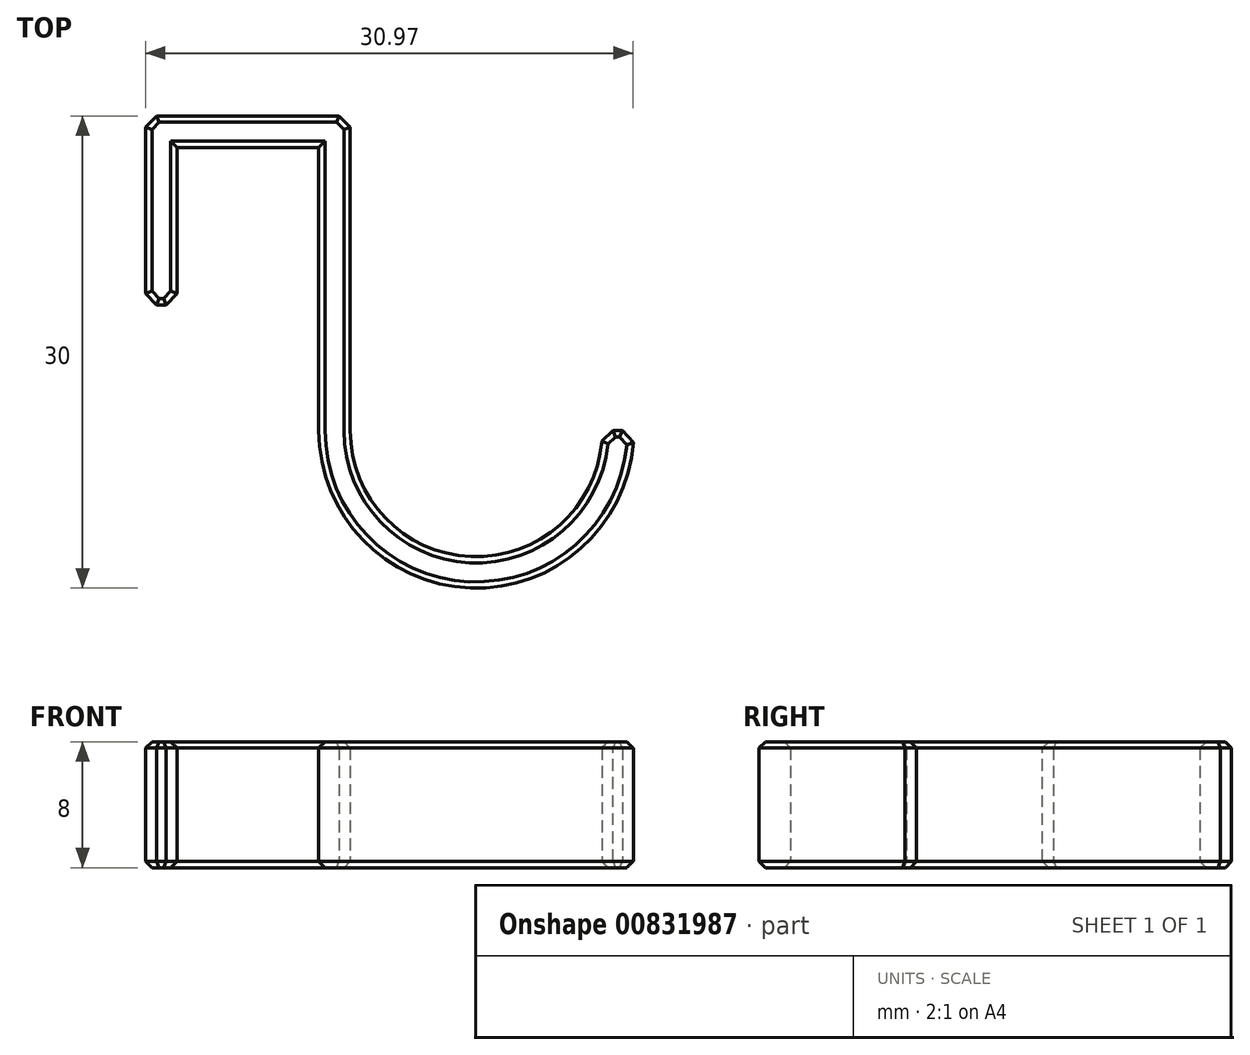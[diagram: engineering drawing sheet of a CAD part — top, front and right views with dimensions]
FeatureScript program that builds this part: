
annotation { "Feature Type Name" : "Feature", "Feature Type Description" : "" }
export const myFeature = defineFeature(function(context is Context, id is Id, definition is map)
    precondition{}
    {
        {
            var Q0;
            Q0=qCreatedBy(makeId("Top.planeOp"),FACE);
            var sketch = newSketch(context, id + "F0", { "sketchPlane" : qUnion([Q0])});
            skLineSegment(sketch, "E0", {"start": v(-19, 8) * mm, "end": v(-19, 18) * mm});
            skLineSegment(sketch, "E1", {"start": v(-19, 18) * mm, "end": v(-10, 18) * mm});
            skLineSegment(sketch, "E2", {"start": v(-10, 18) * mm, "end": v(-10, 0) * mm});
            skLineSegment(sketch, "E3", {"start": v(-19, 8) * mm, "end": v(-21, 8) * mm});
            skLineSegment(sketch, "E4", {"start": v(-21, 8) * mm, "end": v(-21, 20) * mm});
            skLineSegment(sketch, "E5", {"start": v(-21, 20) * mm, "end": v(-8, 20) * mm});
            skLineSegment(sketch, "E6", {"start": v(-8, 20) * mm, "end": v(-8, 0) * mm});
            skLineSegment(sketch, "E7", {"start": v(8, 0) * mm, "end": v(10, 0) * mm});
            skArc(sketch, "E8", {"start": v(-8, 0) * mm, "mid": v(0, -8) * mm, "end": v(8, 0) * mm});
            skArc(sketch, "E9", {"start": v(-10, 0) * mm, "mid": v(0, -10) * mm, "end": v(10, 0) * mm});
            skLineSegment(sketch, "E10", {"start": v(-19, 18) * mm, "end": v(-21, 18) * mm, "construction": true});
            skLineSegment(sketch, "E11", {"start": v(-10, 18) * mm, "end": v(-8, 18) * mm, "construction": true});
            skLineSegment(sketch, "E12", {"start": v(-10, 18) * mm, "end": v(-10, 20) * mm, "construction": true});
            skSolve(sketch);
        }
        {
            var Q0;
            Q0=makeQuery(id+"F0.imprint","IMPRINT",FACE,{"disambiguationData":[TD([[makeQuery(id+"F0.imprint","IMPRINT",EDGE,{"derivedFrom":sQuery(id+"F0.wireOp",EDGE,"E0")}),1.0]])]});
            extrude(context, id + "F1", {"entities" : qUnion([Q0]), "depth" : 8 * mm, "offsetDistance" : 25 * mm});
        }
        {
            var Q0;
            Q0=makeQuery(id+"F1.opExtrude","SWEPT_EDGE",EDGE,{"disambiguationData":[OSD([sQuery(id+"F0.wireOp",EDGE,"E5"),sQuery(id+"F0.wireOp",EDGE,"E6")])]});
            var Q1;
            Q1=makeQuery(id+"F1.opExtrude","SWEPT_EDGE",EDGE,{"disambiguationData":[OSD([sQuery(id+"F0.wireOp",EDGE,"E4"),sQuery(id+"F0.wireOp",EDGE,"E5")])]});
            var Q2;
            Q2=makeQuery(id+"F1.opExtrude","SWEPT_EDGE",EDGE,{"disambiguationData":[OSD([sQuery(id+"F0.wireOp",EDGE,"E3"),sQuery(id+"F0.wireOp",EDGE,"E4")])]});
            var Q3;
            Q3=makeQuery(id+"F1.opExtrude","SWEPT_EDGE",EDGE,{"disambiguationData":[OSD([sQuery(id+"F0.wireOp",EDGE,"E0"),sQuery(id+"F0.wireOp",EDGE,"E3")])]});
            var Q4;
            Q4=makeQuery(id+"F1.opExtrude","SWEPT_EDGE",EDGE,{"disambiguationData":[OSD([sQuery(id+"F0.wireOp",EDGE,"E7"),sQuery(id+"F0.wireOp",EDGE,"E9")])]});
            var Q5;
            Q5=makeQuery(id+"F1.opExtrude","SWEPT_EDGE",EDGE,{"disambiguationData":[OSD([sQuery(id+"F0.wireOp",EDGE,"E7"),sQuery(id+"F0.wireOp",EDGE,"E8")])]});
            chamfer(context, id + "F2", {"entities" : qUnion([Q0, Q1, Q2, Q3, Q4, Q5]), "width" : 0.7 * mm, "tangentPropagation" : true});
        }
        {
            var Q0;
            Q0=makeQuery(id+"F1.opExtrude","CAP_FACE",FACE,{"disambiguationData":[OSD([sQuery(id+"F0.wireOp",EDGE,"E0"),sQuery(id+"F0.wireOp",EDGE,"E1"),sQuery(id+"F0.wireOp",EDGE,"E2"),sQuery(id+"F0.wireOp",EDGE,"E3"),sQuery(id+"F0.wireOp",EDGE,"E4"),sQuery(id+"F0.wireOp",EDGE,"E5"),sQuery(id+"F0.wireOp",EDGE,"E6"),sQuery(id+"F0.wireOp",EDGE,"E7"),sQuery(id+"F0.wireOp",EDGE,"E8"),sQuery(id+"F0.wireOp",EDGE,"E9")])],"isStart":false});
            var Q1;
            Q1=makeQuery(id+"F1.opExtrude","CAP_FACE",FACE,{"disambiguationData":[OSD([sQuery(id+"F0.wireOp",EDGE,"E0"),sQuery(id+"F0.wireOp",EDGE,"E1"),sQuery(id+"F0.wireOp",EDGE,"E2"),sQuery(id+"F0.wireOp",EDGE,"E3"),sQuery(id+"F0.wireOp",EDGE,"E4"),sQuery(id+"F0.wireOp",EDGE,"E5"),sQuery(id+"F0.wireOp",EDGE,"E6"),sQuery(id+"F0.wireOp",EDGE,"E7"),sQuery(id+"F0.wireOp",EDGE,"E8"),sQuery(id+"F0.wireOp",EDGE,"E9")])],"isStart":true});
            chamfer(context, id + "F3", {"entities" : qUnion([Q0, Q1]), "width" : 0.4 * mm, "tangentPropagation" : true});
        }
    });
